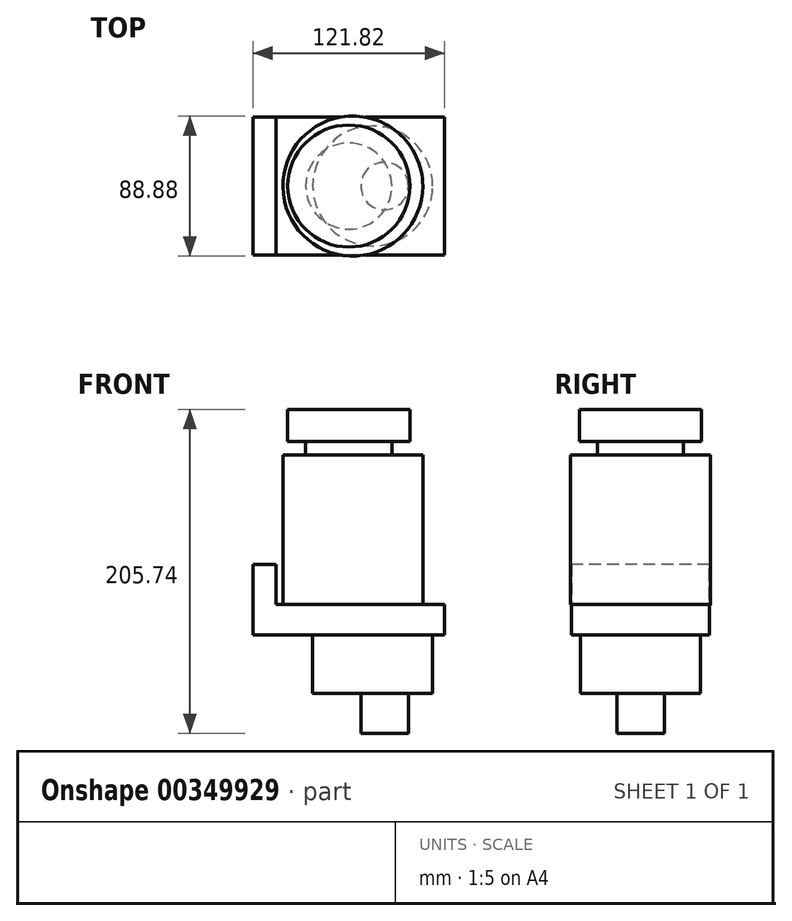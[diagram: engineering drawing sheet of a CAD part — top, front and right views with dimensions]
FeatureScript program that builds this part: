
annotation { "Feature Type Name" : "Feature", "Feature Type Description" : "" }
export const myFeature = defineFeature(function(context is Context, id is Id, definition is map)
    precondition{}
    {
        {
            var Q0;
            Q0=qCreatedBy(makeId("Top.planeOp"),FACE);
            var sketch = newSketch(context, id + "F0", { "sketchPlane" : qUnion([Q0])});
            skCircle(sketch, "E0", {"center": v(2.56, 0) * mm, "radius": 44.44 * mm});
            skSolve(sketch);
        }
        {
            var Q0;
            Q0 = qSketchRegion(id + "F0", true);
            extrude(context, id + "F1", {"entities" : qUnion([Q0]), "depth" : 95 * mm, "offsetDistance" : 25.4 * mm});
        }
        {
            var Q0;
            Q0=makeQuery(id+"F1.opExtrude","CAP_FACE",FACE,{"disambiguationData":[OSD([sQuery(id+"F0.wireOp",EDGE,"E0")])],"isStart":true});
            var sketch = newSketch(context, id + "F2", { "sketchPlane" : qUnion([Q0])});
            skLineSegment(sketch, "E1.bottom", {"start": v(60.9, -43.76) * mm, "end": v(-60.9, -43.76) * mm});
            skLineSegment(sketch, "E1.top", {"start": v(60.9, 43.76) * mm, "end": v(-60.9, 43.76) * mm});
            skLineSegment(sketch, "E1.left", {"start": v(60.9, -43.76) * mm, "end": v(60.9, 43.76) * mm});
            skLineSegment(sketch, "E1.right", {"start": v(-60.9, -43.76) * mm, "end": v(-60.9, 43.76) * mm});
            skPoint(sketch, "E1.middle", {"position": v(0, 0) * mm});
            skSolve(sketch);
        }
        {
            var Q0;
            Q0 = qSketchRegion(id + "F2", true);
            extrude(context, id + "F3", {"entities" : qUnion([Q0]), "operationType" : NewBodyOperationType.ADD, "depth" : 19.3 * mm, "offsetDistance" : 25.4 * mm});
        }
        {
            var Q0;
            Q0=makeQuery(id+"F3.opExtrude","CAP_FACE",FACE,{"disambiguationData":[OSD([sQuery(id+"F2.wireOp",EDGE,"E1.bottom"),sQuery(id+"F2.wireOp",EDGE,"E1.top"),sQuery(id+"F2.wireOp",EDGE,"E1.left"),sQuery(id+"F2.wireOp",EDGE,"E1.right")])],"isStart":false});
            var sketch = newSketch(context, id + "F4", { "sketchPlane" : qUnion([Q0])});
            skCircle(sketch, "E2", {"center": v(15.19, 0) * mm, "radius": 38.08 * mm});
            skSolve(sketch);
        }
        {
            var Q0;
            Q0 = qSketchRegion(id + "F4", true);
            extrude(context, id + "F5", {"entities" : qUnion([Q0]), "operationType" : NewBodyOperationType.ADD, "depth" : 37.08 * mm, "offsetDistance" : 25.4 * mm});
        }
        {
            var Q0;
            Q0=makeQuery(id+"F5.opExtrude","CAP_FACE",FACE,{"disambiguationData":[OSD([sQuery(id+"F4.wireOp",EDGE,"E2")])],"isStart":false});
            var sketch = newSketch(context, id + "F6", { "sketchPlane" : qUnion([Q0])});
            skCircle(sketch, "E3", {"center": v(22.7, 0) * mm, "radius": 15.07 * mm});
            skSolve(sketch);
        }
        {
            var Q0;
            Q0 = qSketchRegion(id + "F6", true);
            extrude(context, id + "F7", {"entities" : qUnion([Q0]), "operationType" : NewBodyOperationType.ADD, "depth" : 25.4 * mm, "offsetDistance" : 25.4 * mm});
        }
        {
            var Q0;
            Q0=makeQuery(id+"F1.opExtrude","CAP_FACE",FACE,{"disambiguationData":[OSD([sQuery(id+"F0.wireOp",EDGE,"E0")])],"isStart":false});
            var sketch = newSketch(context, id + "F8", { "sketchPlane" : qUnion([Q0])});
            skCircle(sketch, "E4", {"center": v(0, 0) * mm, "radius": 27.35 * mm});
            skSolve(sketch);
        }
        {
            var Q0;
            Q0 = qSketchRegion(id + "F8", true);
            extrude(context, id + "F9", {"entities" : qUnion([Q0]), "operationType" : NewBodyOperationType.ADD, "depth" : 8.64 * mm, "offsetDistance" : 25.4 * mm});
        }
        {
            var Q0;
            Q0=makeQuery(id+"F9.opExtrude","CAP_FACE",FACE,{"disambiguationData":[OSD([sQuery(id+"F8.wireOp",EDGE,"E4")])],"isStart":false});
            var sketch = newSketch(context, id + "F10", { "sketchPlane" : qUnion([Q0])});
            skCircle(sketch, "E5", {"center": v(0, 0) * mm, "radius": 38.76 * mm});
            skSolve(sketch);
        }
        {
            var Q0;
            Q0 = qSketchRegion(id + "F10", true);
            extrude(context, id + "F11", {"entities" : qUnion([Q0]), "operationType" : NewBodyOperationType.ADD, "depth" : 20.32 * mm, "offsetDistance" : 25.4 * mm});
        }
        {
            var Q0;
            {var subQ0=sQuery(id+"F2.wireOp",EDGE,"E1.bottom");var subQ2=sQuery(id+"F2.wireOp",EDGE,"E1.top");var subQ3=sQuery(id+"F2.wireOp",EDGE,"E1.right");Q0=makeQuery(id+"F3.boolean.opBoolean","SPLIT",FACE,{"disambiguationData":[TD([makeQuery(id+"F3.opExtrude","SWEPT_FACE",FACE,{"disambiguationData":[OSD([subQ3])]})])],"derivedFrom":makeQuery(id+"F3.opExtrude","CAP_FACE",FACE,{"disambiguationData":[OSD([subQ0,subQ2,sQuery(id+"F2.wireOp",EDGE,"E1.left"),subQ3])],"isStart":true})});}
            var sketch = newSketch(context, id + "F12", { "sketchPlane" : qUnion([Q0])});
            skLineSegment(sketch, "E6.bottom", {"start": v(-60.9, 43.76) * mm, "end": v(-46.17, 43.76) * mm});
            skLineSegment(sketch, "E6.top", {"start": v(-60.9, -43.76) * mm, "end": v(-46.17, -43.76) * mm});
            skLineSegment(sketch, "E6.left", {"start": v(-60.9, 43.76) * mm, "end": v(-60.9, -43.76) * mm});
            skLineSegment(sketch, "E6.right", {"start": v(-46.17, 43.76) * mm, "end": v(-46.17, -43.76) * mm});
            skSolve(sketch);
        }
        {
            var Q0;
            Q0 = qSketchRegion(id + "F12", true);
            extrude(context, id + "F13", {"entities" : qUnion([Q0]), "operationType" : NewBodyOperationType.ADD, "depth" : 25.4 * mm, "offsetDistance" : 25.4 * mm});
        }
    });
